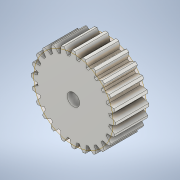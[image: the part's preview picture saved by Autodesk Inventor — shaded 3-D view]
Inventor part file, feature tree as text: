
AUTODESK INVENTOR PART (.ipt)
format: ipt  version: 2021 (Build 250183000, 183)  size: 276,992 bytes
history: native  units: mm (DEFAULTED — no unit token found)
features: plane x3, other x3, sketch x3, extrude x1, hole x1
ambient origin geometry x8: Origin, YZ Plane, XZ Plane, XY Plane, X Axis, Y Axis, Z Axis, Center Point
bodies: Solid1 (feature_tree)
feature tree (11):
  extrude  "Extrusion1"  Depth=8.0mm TaperAngle=0.0deg
  plane  "Work Plane2"
  plane  "Work Plane8"
  plane  "Work Plane9"
  other  "Spur Gear"
  hole  "Hole1"  [1 undecoded]
  sketch  "Sketch1"  dims[d0=20.48mm d1=8.0mm d2=0.0mm]
  sketch  "Sketch2"  dims[d3=19.2mm d4=10.0mm d5=0.0mm]
  other  "Srf1"
  sketch  "Sketch3"  dims[d16=28.8mm d17=0.0mm d34=1.308997mm d39=0.0mm d41=0.0mm d43=28.8mm d46=28.8mm d47=0.0mm d48=0.0mm d49=3.0mm d50=3.0mm d51=6.0mm d52=4.0mm d53=2.0mm d54=90.0deg d55=8.0mm d56=20.594885mm]
  other  "Pitch Diameter"
note: 1 required parameter value undecoded (feature->parameter linkage not recoverable at this tier; creation-order binding heuristic only, values carry confidence <= 0.55)
